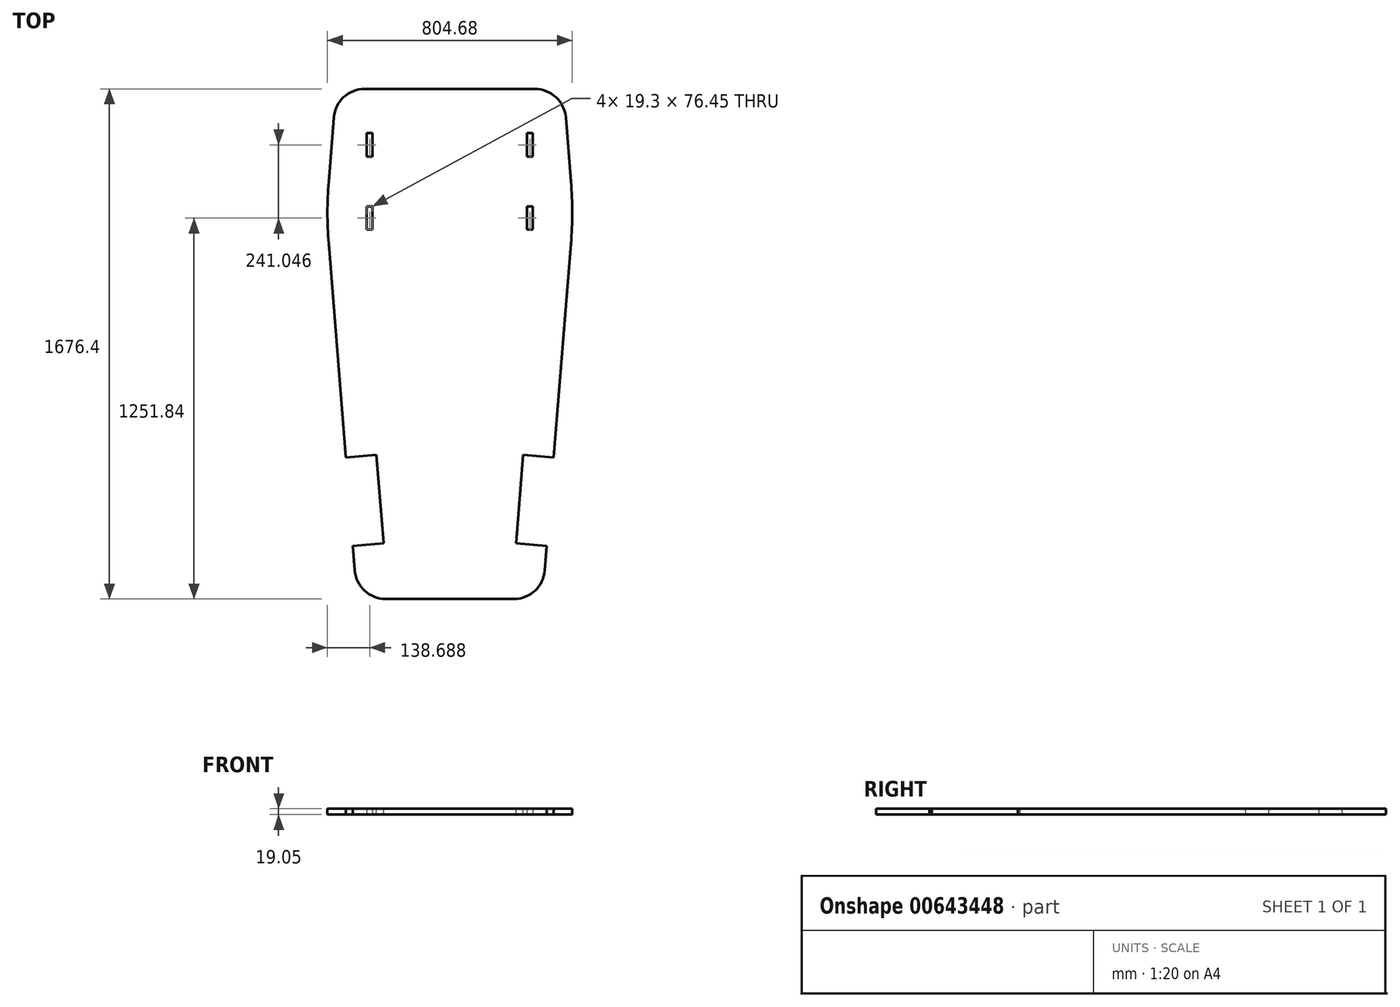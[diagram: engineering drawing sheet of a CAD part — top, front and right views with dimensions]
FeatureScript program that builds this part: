
annotation { "Feature Type Name" : "Feature", "Feature Type Description" : "" }
export const myFeature = defineFeature(function(context is Context, id is Id, definition is map)
    precondition{}
    {
        {
            var Q0;
            Q0=qCreatedBy(makeId("Top.planeOp"),FACE);
            var sketch = newSketch(context, id + "F0", { "sketchPlane" : qUnion([Q0])});
            skLineSegment(sketch, "E0", {"start": v(0, 0) * mm, "end": v(304.8, 0) * mm});
            skLineSegment(sketch, "E1", {"start": v(0, 0) * mm, "end": v(-304.8, 0) * mm});
            skLineSegment(sketch, "E2", {"start": v(0, 1270) * mm, "end": v(-406.4, 1270) * mm, "construction": true});
            skLineSegment(sketch, "E3.MirrorCS", {"start": v(0, 1270) * mm, "end": v(406.4, 1270) * mm, "construction": true});
            skLineSegment(sketch, "E4", {"start": v(-304.8, 0) * mm, "end": v(-406.4, 1270) * mm});
            skLineSegment(sketch, "E5", {"start": v(304.8, 0) * mm, "end": v(406.4, 1270) * mm});
            skLineSegment(sketch, "E6", {"start": v(0, 1270) * mm, "end": v(0, 1676.4) * mm, "construction": true});
            skLineSegment(sketch, "E7.MirrorCS", {"start": v(-373.89, 1676.4) * mm, "end": v(-406.4, 1270) * mm});
            skLineSegment(sketch, "E8.MirrorCS", {"start": v(373.89, 1676.4) * mm, "end": v(406.4, 1270) * mm});
            skLineSegment(sketch, "E9", {"start": v(0, 1676.4) * mm, "end": v(-373.89, 1676.4) * mm});
            skLineSegment(sketch, "E10", {"start": v(0, 1676.4) * mm, "end": v(373.89, 1676.4) * mm});
            skPoint(sketch, "E11.orphan", {"position": v(304.8, 2540) * mm});
            skPoint(sketch, "E12.orphan", {"position": v(-304.8, 2540) * mm});
            skLineSegment(sketch, "E13", {"start": v(0, 1270) * mm, "end": v(0, 1213.6) * mm});
            skLineSegment(sketch, "E14", {"start": v(0, 1213.6) * mm, "end": v(273.3, 1213.6) * mm, "construction": true});
            skLineSegment(sketch, "E15.MirrorCS", {"start": v(0, 1213.6) * mm, "end": v(-273.3, 1213.6) * mm, "construction": true});
            skLineSegment(sketch, "E16", {"start": v(-273.3, 1213.6) * mm, "end": v(-273.3, 1531.1) * mm, "construction": true});
            skLineSegment(sketch, "E17", {"start": v(-273.3, 1531.1) * mm, "end": v(-254, 1531.1) * mm});
            skLineSegment(sketch, "E18", {"start": v(-254, 1531.1) * mm, "end": v(-254, 1454.66) * mm});
            skLineSegment(sketch, "E19", {"start": v(-254, 1454.66) * mm, "end": v(-273.3, 1454.66) * mm});
            skLineSegment(sketch, "E20", {"start": v(-273.3, 1213.6) * mm, "end": v(-273.3, 1290.06) * mm});
            skLineSegment(sketch, "E21", {"start": v(-273.3, 1290.06) * mm, "end": v(-254, 1290.06) * mm});
            skLineSegment(sketch, "E22", {"start": v(-254, 1290.06) * mm, "end": v(-254, 1213.6) * mm});
            skLineSegment(sketch, "E23", {"start": v(-273.3, 1454.66) * mm, "end": v(-273.3, 1531.1) * mm});
            skLineSegment(sketch, "E24.MirrorCS", {"start": v(254, 1531.1) * mm, "end": v(254, 1454.66) * mm});
            skLineSegment(sketch, "E25.MirrorCS", {"start": v(273.3, 1454.66) * mm, "end": v(273.3, 1531.1) * mm});
            skLineSegment(sketch, "E26.MirrorCS", {"start": v(254, 1454.66) * mm, "end": v(273.3, 1454.66) * mm});
            skLineSegment(sketch, "E27.MirrorCS", {"start": v(273.3, 1531.1) * mm, "end": v(254, 1531.1) * mm});
            skLineSegment(sketch, "E28.MirrorCS", {"start": v(273.3, 1213.6) * mm, "end": v(273.3, 1290.06) * mm});
            skLineSegment(sketch, "E29.MirrorCS", {"start": v(273.3, 1290.06) * mm, "end": v(254, 1290.06) * mm});
            skLineSegment(sketch, "E30.MirrorCS", {"start": v(254, 1290.06) * mm, "end": v(254, 1213.6) * mm});
            skLineSegment(sketch, "E31", {"start": v(273.3, 1213.6) * mm, "end": v(254, 1213.6) * mm});
            skLineSegment(sketch, "E32", {"start": v(-254, 1213.6) * mm, "end": v(-273.3, 1213.6) * mm});
            skLineSegment(sketch, "E33", {"start": v(-254, 1531.1) * mm, "end": v(254, 1531.1) * mm, "construction": true});
            skLineSegment(sketch, "E34", {"start": v(-273.3, 1213.6) * mm, "end": v(-401.89, 1213.6) * mm, "construction": true});
            skLineSegment(sketch, "E35", {"start": v(273.3, 1454.66) * mm, "end": v(273.3, 1290.06) * mm, "construction": true});
            skSolve(sketch);
        }
        {
            var Q0;
            Q0=makeQuery(id+"F0.imprint","IMPRINT",FACE,{"disambiguationData":[TD([[makeQuery(id+"F0.imprint","IMPRINT",EDGE,{"derivedFrom":sQuery(id+"F0.wireOp",EDGE,"E0")}),1.0]])]});
            extrude(context, id + "F1", {"entities" : qUnion([Q0]), "depth" : 19.05 * mm, "offsetDistance" : 25.4 * mm});
        }
        {
            var Q0;
            Q0=makeQuery(id+"F1.opExtrude","SWEPT_EDGE",EDGE,{"disambiguationData":[OSD([sQuery(id+"F0.wireOp",EDGE,"E1"),sQuery(id+"F0.wireOp",EDGE,"E4")])]});
            var Q1;
            Q1=makeQuery(id+"F1.opExtrude","SWEPT_EDGE",EDGE,{"disambiguationData":[OSD([sQuery(id+"F0.wireOp",EDGE,"E0"),sQuery(id+"F0.wireOp",EDGE,"E5")])]});
            var Q2;
            Q2=makeQuery(id+"F1.opExtrude","SWEPT_EDGE",EDGE,{"disambiguationData":[OSD([sQuery(id+"F0.wireOp",EDGE,"E7.MirrorCS"),sQuery(id+"F0.wireOp",EDGE,"E9")])]});
            var Q3;
            Q3=makeQuery(id+"F1.opExtrude","SWEPT_EDGE",EDGE,{"disambiguationData":[OSD([sQuery(id+"F0.wireOp",EDGE,"E8.MirrorCS"),sQuery(id+"F0.wireOp",EDGE,"E10")])]});
            fillet(context, id + "F2", {"entities" : qUnion([Q0, Q1, Q2, Q3]), "radius" : 101.6 * mm, "tangentPropagation" : true, "allowEdgeOverflow" : false});
        }
        {
            var Q0;
            Q0=makeQuery(id+"F1.opExtrude","SWEPT_EDGE",EDGE,{"disambiguationData":[OSD([sQuery(id+"F0.wireOp",EDGE,"E4"),sQuery(id+"F0.wireOp",EDGE,"E7.MirrorCS")])]});
            var Q1;
            Q1=makeQuery(id+"F1.opExtrude","SWEPT_EDGE",EDGE,{"disambiguationData":[OSD([sQuery(id+"F0.wireOp",EDGE,"E5"),sQuery(id+"F0.wireOp",EDGE,"E8.MirrorCS")])]});
            fillet(context, id + "F3", {"entities" : qUnion([Q0, Q1]), "radius" : 1270 * mm, "tangentPropagation" : true, "allowEdgeOverflow" : false});
        }
        {
            var Q0;
            Q0=makeQuery(id+"F1.opExtrude","CAP_FACE",FACE,{"disambiguationData":[OSD([sQuery(id+"F0.wireOp",EDGE,"E0"),sQuery(id+"F0.wireOp",EDGE,"E1"),sQuery(id+"F0.wireOp",EDGE,"E4"),sQuery(id+"F0.wireOp",EDGE,"E5"),sQuery(id+"F0.wireOp",EDGE,"E7.MirrorCS"),sQuery(id+"F0.wireOp",EDGE,"E8.MirrorCS"),sQuery(id+"F0.wireOp",EDGE,"E9"),sQuery(id+"F0.wireOp",EDGE,"E10"),sQuery(id+"F0.wireOp",EDGE,"E17"),sQuery(id+"F0.wireOp",EDGE,"E18"),sQuery(id+"F0.wireOp",EDGE,"E19"),sQuery(id+"F0.wireOp",EDGE,"E21"),sQuery(id+"F0.wireOp",EDGE,"E22"),sQuery(id+"F0.wireOp",EDGE,"E20"),sQuery(id+"F0.wireOp",EDGE,"E23"),sQuery(id+"F0.wireOp",EDGE,"E24.MirrorCS"),sQuery(id+"F0.wireOp",EDGE,"E25.MirrorCS"),sQuery(id+"F0.wireOp",EDGE,"E26.MirrorCS"),sQuery(id+"F0.wireOp",EDGE,"E27.MirrorCS"),sQuery(id+"F0.wireOp",EDGE,"E29.MirrorCS"),sQuery(id+"F0.wireOp",EDGE,"E28.MirrorCS"),sQuery(id+"F0.wireOp",EDGE,"E30.MirrorCS"),sQuery(id+"F0.wireOp",EDGE,"E31"),sQuery(id+"F0.wireOp",EDGE,"E32")])],"isStart":false});
            var sketch = newSketch(context, id + "F4", { "sketchPlane" : qUnion([Q0])});
            skPoint(sketch, "E36.endSnap0", {"position": v(0, 0) * mm});
            skPoint(sketch, "E37.endSnap0", {"position": v(-355.29, 631.11) * mm});
            skLineSegment(sketch, "E38.MirrorCS", {"start": v(-241.08, 473.54) * mm, "end": v(-217.79, 182.37) * mm});
            skLineSegment(sketch, "E39.MirrorCS", {"start": v(-352.6, 464.62) * mm, "end": v(-329.3, 173.45) * mm});
            skLineSegment(sketch, "E40.MirrorCS", {"start": v(-217.79, 182.37) * mm, "end": v(-329.3, 173.45) * mm});
            skLineSegment(sketch, "E41.MirrorCS", {"start": v(-241.08, 473.54) * mm, "end": v(-352.6, 464.62) * mm});
            skLineSegment(sketch, "E42.MirrorCS", {"start": v(241.08, 473.54) * mm, "end": v(217.79, 182.37) * mm});
            skLineSegment(sketch, "E43.MirrorCS", {"start": v(217.79, 182.37) * mm, "end": v(329.3, 173.45) * mm});
            skLineSegment(sketch, "E44.MirrorCS", {"start": v(352.6, 464.62) * mm, "end": v(329.3, 173.45) * mm});
            skLineSegment(sketch, "E45.MirrorCS", {"start": v(241.08, 473.54) * mm, "end": v(352.6, 464.62) * mm});
            skSolve(sketch);
        }
        {
            var Q0;
            {var subQ0=sQuery(id+"F4.wireOp",EDGE,"E38.MirrorCS");Q0=makeQuery(id+"F4.imprint","IMPRINT",FACE,{"disambiguationData":[TD([[makeQuery(id+"F4.imprint","IMPRINT",EDGE,{"derivedFrom":subQ0}),-1.0]])]});}
            var Q1;
            {var subQ0=sQuery(id+"F4.wireOp",EDGE,"E42.MirrorCS");Q1=makeQuery(id+"F4.imprint","IMPRINT",FACE,{"disambiguationData":[TD([[makeQuery(id+"F4.imprint","IMPRINT",EDGE,{"derivedFrom":subQ0}),1.0]])]});}
            extrude(context, id + "F5", {"entities" : qUnion([Q0, Q1]), "operationType" : NewBodyOperationType.REMOVE, "oppositeDirection" : true, "depth" : 187.96 * mm, "offsetDistance" : 25.4 * mm});
        }
    });
